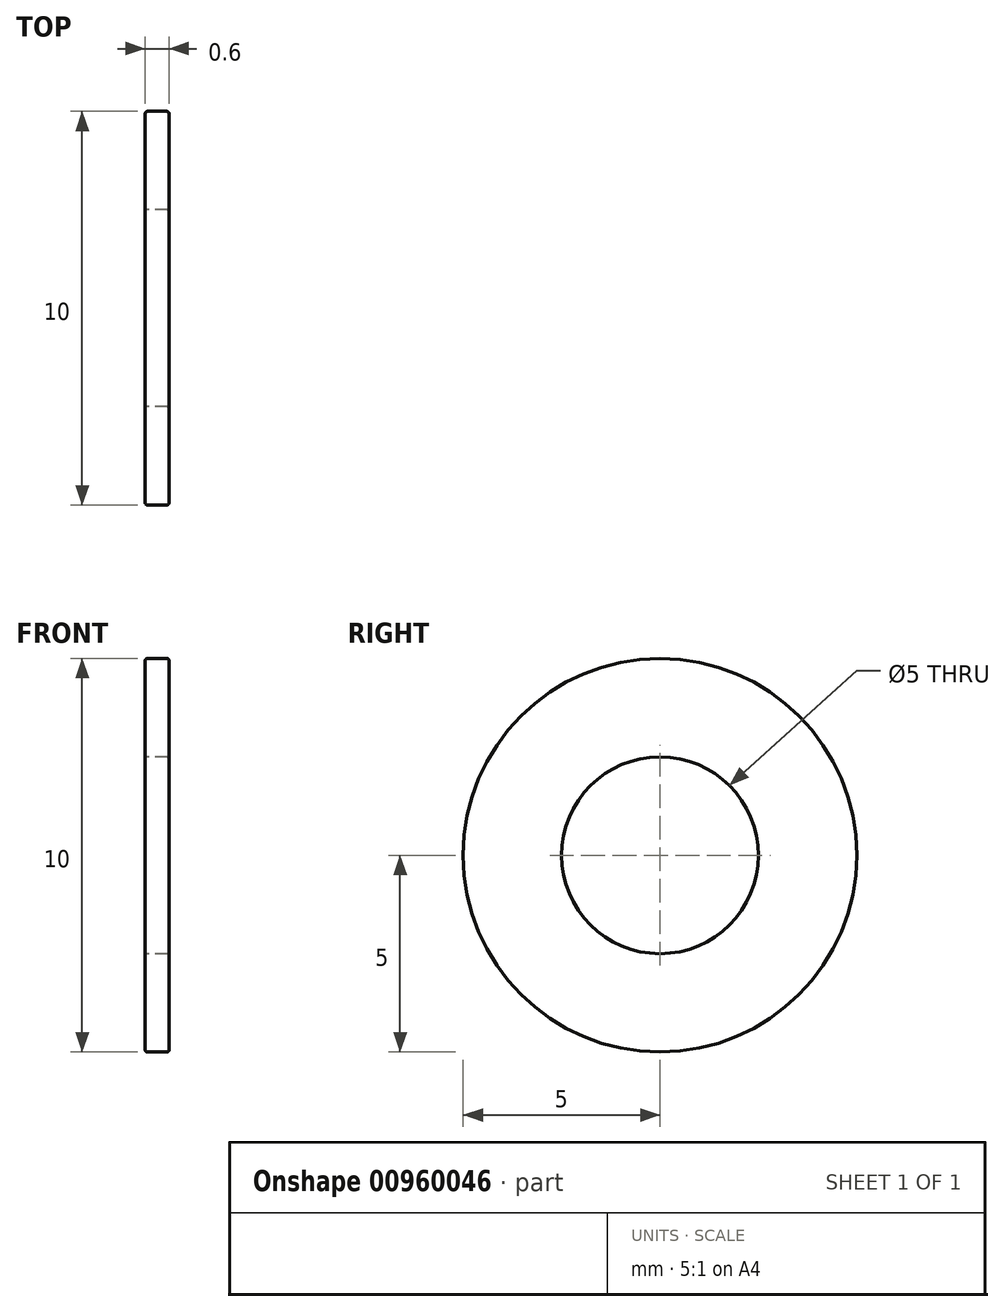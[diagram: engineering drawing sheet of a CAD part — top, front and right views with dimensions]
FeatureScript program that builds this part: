
annotation { "Feature Type Name" : "Feature", "Feature Type Description" : "" }
export const myFeature = defineFeature(function(context is Context, id is Id, definition is map)
    precondition{}
    {
        {
            var Q0;
            Q0=qCreatedBy(makeId("Right.planeOp"),FACE);
            var sketch = newSketch(context, id + "F0", { "sketchPlane" : qUnion([Q0])});
            skCircle(sketch, "E0", {"center": v(0, 0) * mm, "radius": 2.5 * mm});
            skCircle(sketch, "E1", {"center": v(0, 0) * mm, "radius": 5 * mm});
            skSolve(sketch);
        }
        {
            var Q0;
            Q0 = qSketchRegion(id + "F0", true);
            extrude(context, id + "F1", {"entities" : qUnion([Q0]), "depth" : 0.6 * mm, "offsetDistance" : 25 * mm});
        }
        {
            var Q0;
            Q0=makeQuery(id+"F1.opExtrude","CAP_EDGE",EDGE,{"disambiguationData":[OSD([sQuery(id+"F0.wireOp",EDGE,"E1")])],"isStart":false});
            var Q1;
            Q1=makeQuery(id+"F1.opExtrude","CAP_EDGE",EDGE,{"disambiguationData":[OSD([sQuery(id+"F0.wireOp",EDGE,"E1")])],"isStart":true});
            var Q2;
            Q2=makeQuery(id+"F1.opExtrude","CAP_EDGE",EDGE,{"disambiguationData":[OSD([sQuery(id+"F0.wireOp",EDGE,"E0")])],"isStart":true});
            var Q3;
            Q3=makeQuery(id+"F1.opExtrude","CAP_EDGE",EDGE,{"disambiguationData":[OSD([sQuery(id+"F0.wireOp",EDGE,"E0")])],"isStart":false});
            fillet(context, id + "F2", {"entities" : qUnion([Q0, Q1, Q2, Q3]), "radius" : 0.05 * mm, "tangentPropagation" : true, "allowEdgeOverflow" : false});
        }
    });
